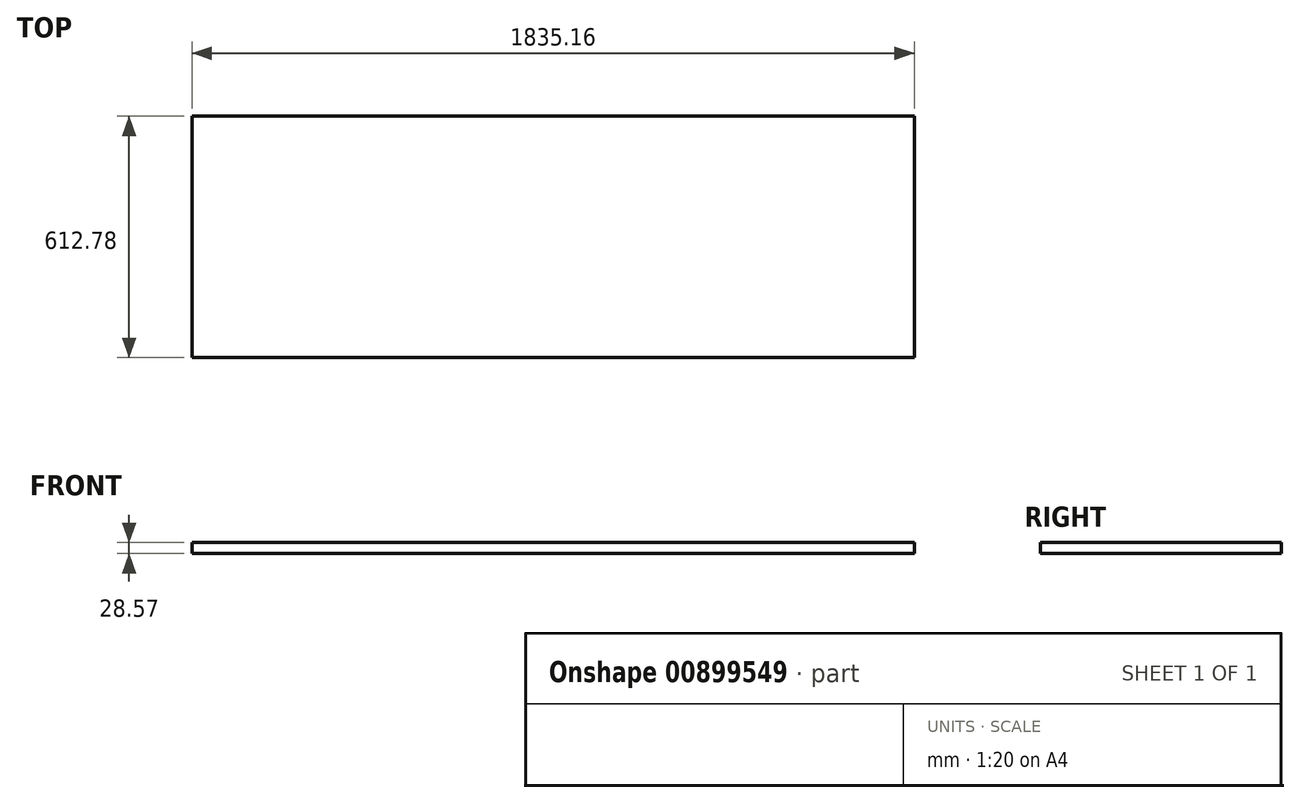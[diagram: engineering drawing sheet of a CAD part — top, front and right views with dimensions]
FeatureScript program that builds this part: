
annotation { "Feature Type Name" : "Feature", "Feature Type Description" : "" }
export const myFeature = defineFeature(function(context is Context, id is Id, definition is map)
    precondition{}
    {
        {
            var Q0;
            Q0=qCreatedBy(makeId("Top.planeOp"),FACE);
            var sketch = newSketch(context, id + "F0", { "sketchPlane" : qUnion([Q0])});
            skLineSegment(sketch, "E0.bottom", {"start": v(-917.58, 306.39) * mm, "end": v(917.58, 306.39) * mm});
            skLineSegment(sketch, "E0.top", {"start": v(-917.58, -306.39) * mm, "end": v(917.58, -306.39) * mm});
            skLineSegment(sketch, "E0.left", {"start": v(-917.58, 306.39) * mm, "end": v(-917.58, -306.39) * mm});
            skLineSegment(sketch, "E0.right", {"start": v(917.58, 306.39) * mm, "end": v(917.58, -306.39) * mm});
            skPoint(sketch, "E0.middle", {"position": v(0, 0) * mm});
            skSolve(sketch);
        }
        {
            var Q0;
            Q0=makeQuery(id+"F0.imprint","IMPRINT",FACE,{"disambiguationData":[TD([[makeQuery(id+"F0.imprint","IMPRINT",EDGE,{"derivedFrom":sQuery(id+"F0.wireOp",EDGE,"E0.bottom")}),-1.0]])]});
            extrude(context, id + "F1", {"entities" : qUnion([Q0]), "depth" : 28.57 * mm, "offsetDistance" : 25.4 * mm});
        }
    });
